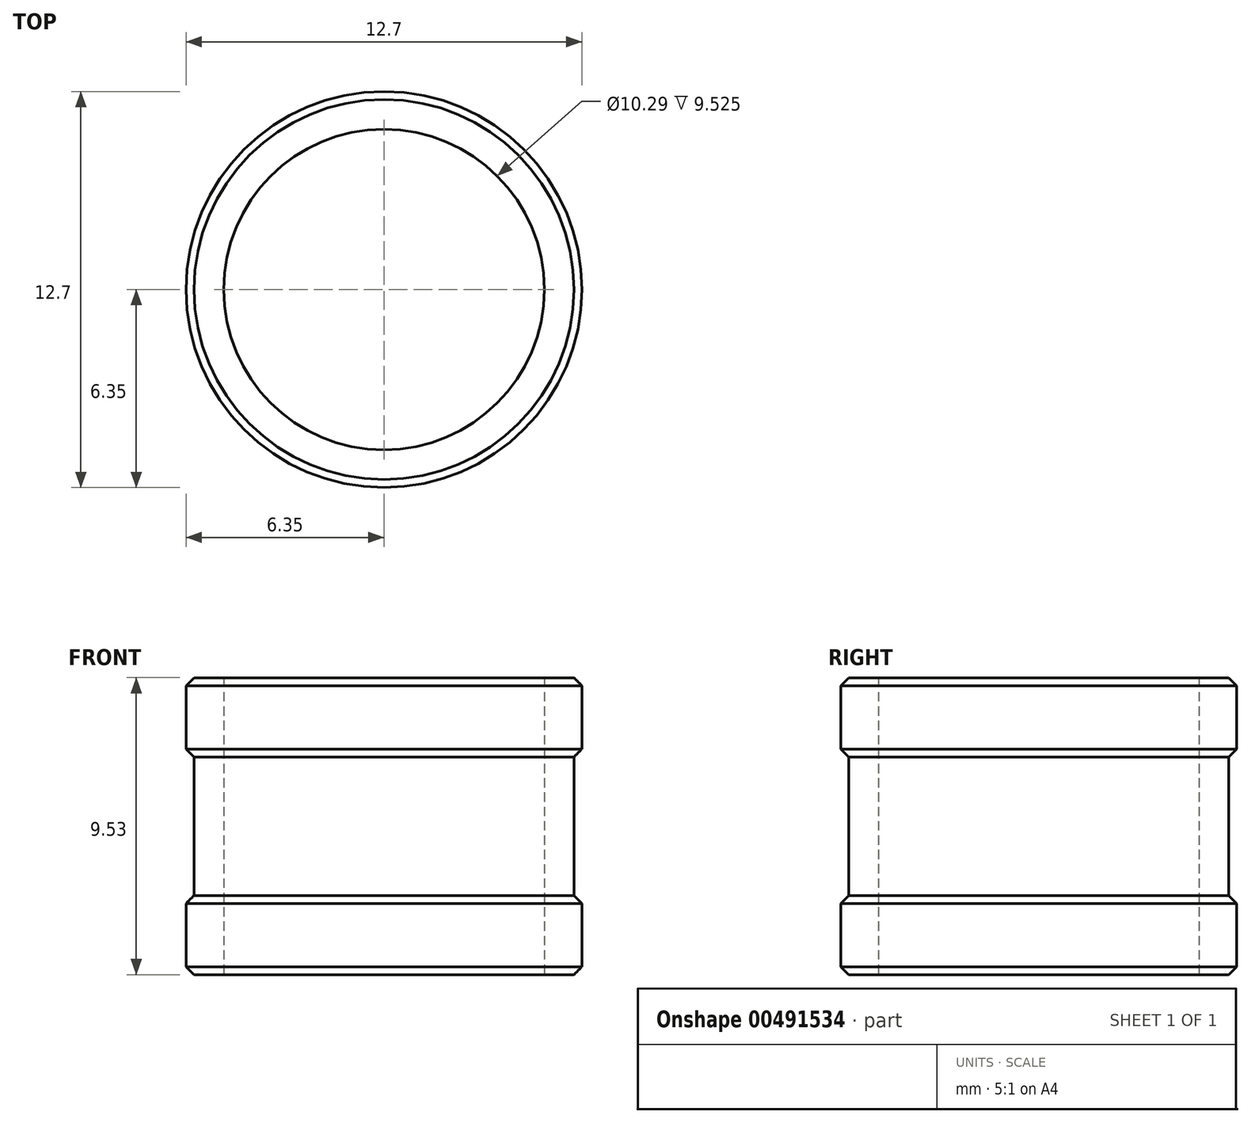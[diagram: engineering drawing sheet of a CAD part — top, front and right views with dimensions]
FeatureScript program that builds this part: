
annotation { "Feature Type Name" : "Feature", "Feature Type Description" : "" }
export const myFeature = defineFeature(function(context is Context, id is Id, definition is map)
    precondition{}
    {
        {
            var Q0;
            Q0=qCreatedBy(makeId("Top.planeOp"),FACE);
            var sketch = newSketch(context, id + "F0", { "sketchPlane" : qUnion([Q0])});
            skCircle(sketch, "E0", {"center": v(0, 0) * mm, "radius": 5.14 * mm});
            skCircle(sketch, "E1", {"center": v(0, 0) * mm, "radius": 6.1 * mm});
            skSolve(sketch);
        }
        {
            var Q0;
            Q0 = qSketchRegion(id + "F0", true);
            extrude(context, id + "F1", {"entities" : qUnion([Q0]), "depth" : 9.52 * mm});
        }
        {
            var Q0;
            Q0=makeQuery(id+"F1.opExtrude","CAP_FACE",FACE,{"disambiguationData":[OSD([sQuery(id+"F0.wireOp",EDGE,"E0"),sQuery(id+"F0.wireOp",EDGE,"E1")])],"isStart":false});
            var sketch = newSketch(context, id + "F2", { "sketchPlane" : qUnion([Q0])});
            skCircle(sketch, "E2", {"center": v(0, 0) * mm, "radius": 6.35 * mm});
            skCircle(sketch, "E3", {"center": v(0, 0) * mm, "radius": 5.14 * mm});
            skSolve(sketch);
        }
        {
            var Q0;
            Q0 = qSketchRegion(id + "F2", true);
            extrude(context, id + "F3", {"entities" : qUnion([Q0]), "operationType" : NewBodyOperationType.ADD, "oppositeDirection" : true, "depth" : 2.54 * mm});
        }
        {
            var Q0;
            Q0=makeQuery(id+"F1.opExtrude","CAP_FACE",FACE,{"disambiguationData":[OSD([sQuery(id+"F0.wireOp",EDGE,"E0"),sQuery(id+"F0.wireOp",EDGE,"E1")])],"isStart":true});
            var sketch = newSketch(context, id + "F4", { "sketchPlane" : qUnion([Q0])});
            skCircle(sketch, "E4", {"center": v(0, 0) * mm, "radius": 5.14 * mm});
            skCircle(sketch, "E5", {"center": v(0, 0) * mm, "radius": 6.35 * mm});
            skSolve(sketch);
        }
        {
            var Q0;
            Q0 = qSketchRegion(id + "F4", true);
            extrude(context, id + "F5", {"entities" : qUnion([Q0]), "operationType" : NewBodyOperationType.ADD, "oppositeDirection" : true, "depth" : 2.54 * mm});
        }
        {
            var Q0;
            Q0=makeQuery(id+"F3.opExtrude","CAP_EDGE",EDGE,{"disambiguationData":[OSD([sQuery(id+"F2.wireOp",EDGE,"E2")])],"isStart":false});
            var Q1;
            Q1=makeQuery(id+"F3.opExtrude","CAP_EDGE",EDGE,{"disambiguationData":[OSD([sQuery(id+"F2.wireOp",EDGE,"E2")])],"isStart":true});
            var Q2;
            Q2=makeQuery(id+"F5.opExtrude","CAP_EDGE",EDGE,{"disambiguationData":[OSD([sQuery(id+"F4.wireOp",EDGE,"E5")])],"isStart":false});
            var Q3;
            Q3=makeQuery(id+"F5.opExtrude","CAP_EDGE",EDGE,{"disambiguationData":[OSD([sQuery(id+"F4.wireOp",EDGE,"E5")])],"isStart":true});
            chamfer(context, id + "F6", {"entities" : qUnion([Q0, Q1, Q2, Q3]), "width" : 0.25 * mm, "tangentPropagation" : true});
        }
    });
